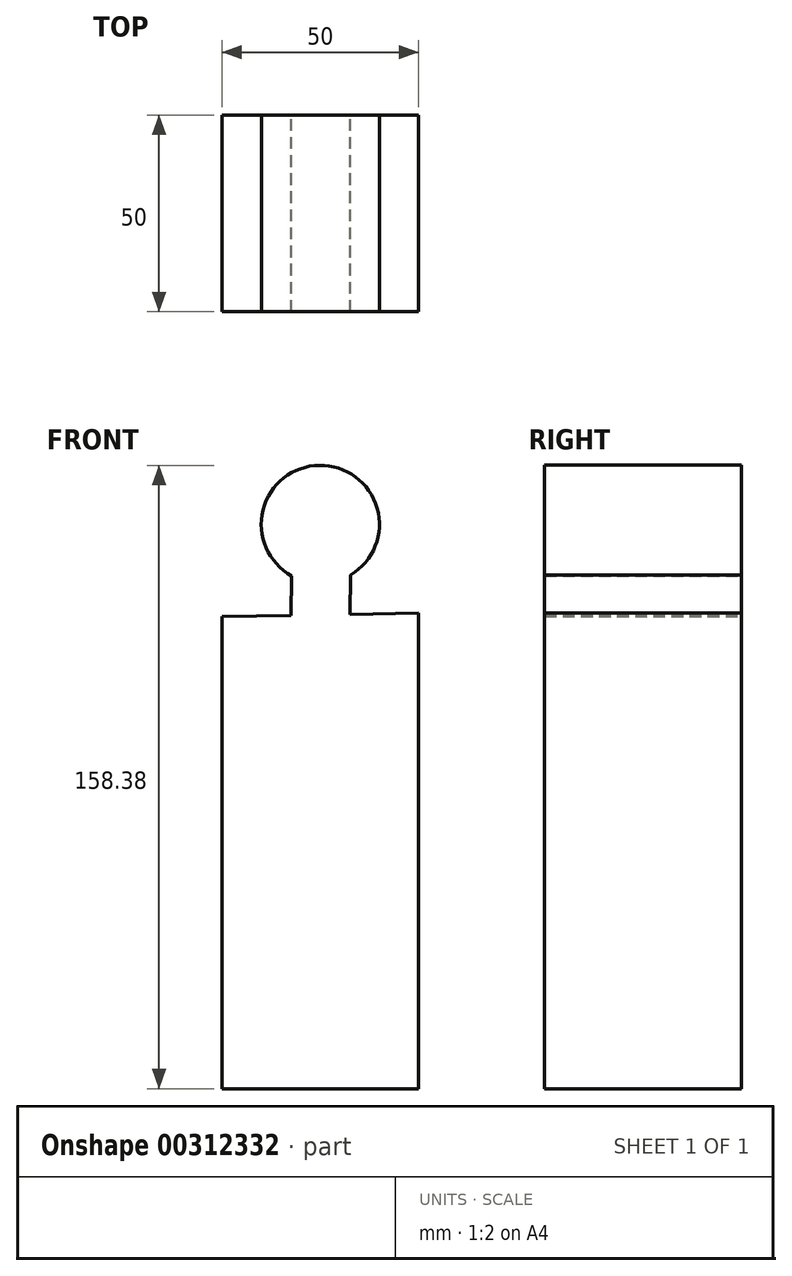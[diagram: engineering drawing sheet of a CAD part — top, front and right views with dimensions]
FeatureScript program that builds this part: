
annotation { "Feature Type Name" : "Feature", "Feature Type Description" : "" }
export const myFeature = defineFeature(function(context is Context, id is Id, definition is map)
    precondition{}
    {
        {
            var Q0;
            Q0=qCreatedBy(makeId("Front.planeOp"),FACE);
            var sketch = newSketch(context, id + "F0", { "sketchPlane" : qUnion([Q0])});
            skLineSegment(sketch, "E0.top", {"start": v(0, -120) * mm, "end": v(50, -120) * mm});
            skLineSegment(sketch, "E0.left", {"start": v(0, 0) * mm, "end": v(0, -120) * mm});
            skLineSegment(sketch, "E0.right", {"start": v(50, 0.8) * mm, "end": v(50, -120) * mm});
            skLineSegment(sketch, "E1", {"start": v(0, 0) * mm, "end": v(17.5, 0.28) * mm});
            skLineSegment(sketch, "E2", {"start": v(25, 0.4) * mm, "end": v(24.85, 10) * mm, "construction": true});
            skLineSegment(sketch, "E3.left", {"start": v(32.71, 10.52) * mm, "end": v(32.5, 0.52) * mm});
            skLineSegment(sketch, "E3.right", {"start": v(17.7, 10.28) * mm, "end": v(17.5, 0.28) * mm});
            skPoint(sketch, "E3.middle", {"position": v(25, 0.4) * mm});
            skPoint(sketch, "E4.orphan", {"position": v(32.3, -9.48) * mm});
            skPoint(sketch, "E5.orphan", {"position": v(17.29, -9.72) * mm});
            skLineSegment(sketch, "E6.trimOffspring", {"start": v(32.5, 0.52) * mm, "end": v(50, 0.8) * mm});
            skCircle(sketch, "E7", {"center": v(25, 23.38) * mm, "radius": 15 * mm});
            skPoint(sketch, "E7.third.point", {"position": v(24.85, 38.38) * mm});
            skLineSegment(sketch, "E8", {"start": v(0, 0) * mm, "end": v(0, 42.22) * mm, "construction": true});
            skLineSegment(sketch, "E9", {"start": v(50, 0.8) * mm, "end": v(50, 43.89) * mm, "construction": true});
            skLineSegment(sketch, "E10", {"start": v(0, 23.38) * mm, "end": v(50, 23.38) * mm, "construction": true});
            skSolve(sketch);
        }
        {
            var Q0;
            Q0=makeQuery(id+"F0.imprint","IMPRINT",FACE,{"disambiguationData":[TD([[makeQuery(id+"F0.imprint","IMPRINT",EDGE,{"derivedFrom":sQuery(id+"F0.wireOp",EDGE,"E3.bottom")}),-1.0]])]});
            var Q1;
            Q1=makeQuery(id+"F0.imprint","IMPRINT",FACE,{"disambiguationData":[TD([[makeQuery(id+"F0.imprint","IMPRINT",EDGE,{"derivedFrom":sQuery(id+"F0.wireOp",EDGE,"E0.top")}),1.0]])]});
            var Q2;
            Q2=makeQuery(id+"F0.imprint","IMPRINT",FACE,{"disambiguationData":[TD([[makeQuery(id+"F0.imprint","IMPRINT",EDGE,{"derivedFrom":sQuery(id+"F0.wireOp",EDGE,"E3.bottom")}),1.0]])]});
            var Q3;
            {var subQ0=sQuery(id+"F0.wireOp",EDGE,"E7");var subQ1=makeQuery(id+"F0.imprint","INTERSECT",VERTEX,{"derivedFrom":[sQuery(id+"F0.wireOp",EDGE,"E3.left"),subQ0]});Q3=makeQuery(id+"F0.imprint","IMPRINT",FACE,{"disambiguationData":[TD([[makeQuery(id+"F0.imprint","IMPRINT",EDGE,{"disambiguationData":[TD([[subQ1,1.0]])],"derivedFrom":subQ0}),1.0]])]});}
            extrude(context, id + "F1", {"entities" : qUnion([Q0, Q1, Q2, Q3]), "depth" : 50 * mm});
        }
    });
